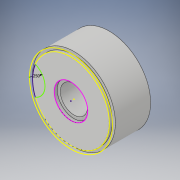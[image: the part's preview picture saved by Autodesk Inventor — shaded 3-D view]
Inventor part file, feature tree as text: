
AUTODESK INVENTOR PART (.ipt)
format: ipt  version: 2018 (Build 220112000, 112)  size: 139,264 bytes
history: native  units: in
note: dims shown in document units (in); Inventor stores cm internally (conversion verified against a paired STEP export)
features: sketch x4, projected_geometry x4, extrude x2
ambient origin geometry x8: Origin, YZ Plane, XZ Plane, XY Plane, X Axis, Y Axis, Z Axis, Center Point
bodies: Solid1 (feature_tree)
feature tree (10):
  extrude  "Extrusion1"  Depth=0.05in
  extrude  "Extrusion2"  Depth=0.05in
  sketch  "Sketch4"  dims[d4=0.57in d5=0.0in]
  sketch  "Sketch5"  dims[d6=0.05in d7=0.0in d9=0.25in]
  sketch  "Sketch1"  dims[d0=0.44in d1=0.05in]
  sketch  "Sketch2"  dims[d2=0.35in d3=0.05in]
  projected_geometry  "Projected Loop1"
  projected_geometry  "Projected Loop2"
  projected_geometry  "Projected Loop3"
  projected_geometry  "Projected Loop4"
